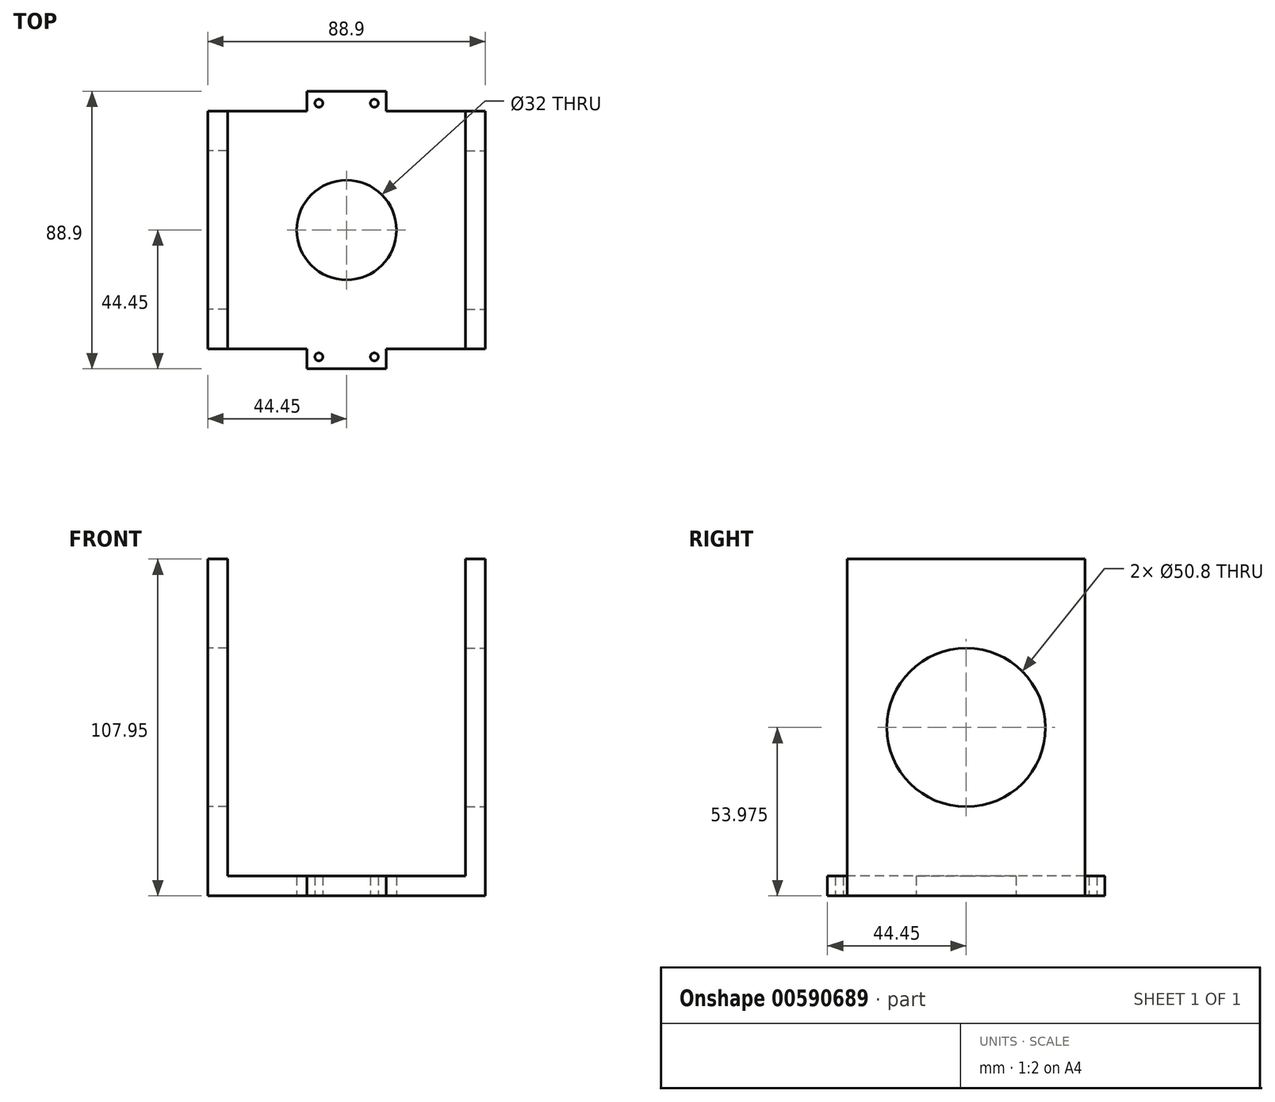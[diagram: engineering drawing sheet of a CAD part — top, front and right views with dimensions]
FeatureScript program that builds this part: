
annotation { "Feature Type Name" : "Feature", "Feature Type Description" : "" }
export const myFeature = defineFeature(function(context is Context, id is Id, definition is map)
    precondition{}
    {
        {
            var Q0;
            Q0=qCreatedBy(makeId("Top.planeOp"),FACE);
            var sketch = newSketch(context, id + "F0", { "sketchPlane" : qUnion([Q0])});
            skLineSegment(sketch, "E0.bottom", {"start": v(0, 0) * mm, "end": v(-88.9, 0) * mm});
            skLineSegment(sketch, "E0.top", {"start": v(0, -76.2) * mm, "end": v(-88.9, -76.2) * mm});
            skLineSegment(sketch, "E0.left", {"start": v(0, 0) * mm, "end": v(0, -76.2) * mm});
            skLineSegment(sketch, "E0.right", {"start": v(-88.9, 0) * mm, "end": v(-88.9, -76.2) * mm});
            skPoint(sketch, "E1.endSnap0", {"position": v(0, -38.1) * mm});
            skCircle(sketch, "E2", {"center": v(-44.45, -38.1) * mm, "radius": 16 * mm});
            skPoint(sketch, "E3.orphan", {"position": v(-44.45, 0) * mm});
            skLineSegment(sketch, "E4", {"start": v(-44.45, -38.1) * mm, "end": v(0, -38.1) * mm});
            skLineSegment(sketch, "E5.bottom", {"start": v(-57.15, 6.35) * mm, "end": v(-31.75, 6.35) * mm});
            skLineSegment(sketch, "E5.left", {"start": v(-57.15, 6.35) * mm, "end": v(-57.15, 0) * mm});
            skLineSegment(sketch, "E5.right", {"start": v(-31.75, 6.35) * mm, "end": v(-31.75, 0) * mm});
            skLineSegment(sketch, "E6.bottom", {"start": v(-57.15, 0) * mm, "end": v(-53.34, 0) * mm});
            skLineSegment(sketch, "E6.top", {"start": v(-54.6, 2.54) * mm, "end": v(-53.34, 2.54) * mm});
            skLineSegment(sketch, "E6.left", {"start": v(-57.15, 0) * mm, "end": v(-57.15, 2.54) * mm});
            skLineSegment(sketch, "E6.right", {"start": v(-53.34, 1.27) * mm, "end": v(-53.34, 2.54) * mm});
            skLineSegment(sketch, "E7.bottom", {"start": v(-31.75, 0) * mm, "end": v(-35.56, 0) * mm});
            skLineSegment(sketch, "E7.top", {"start": v(-34.3, 2.54) * mm, "end": v(-35.56, 2.54) * mm});
            skLineSegment(sketch, "E7.left", {"start": v(-31.75, 0) * mm, "end": v(-31.75, 2.54) * mm});
            skLineSegment(sketch, "E7.right", {"start": v(-35.56, 1.27) * mm, "end": v(-35.56, 2.54) * mm});
            skCircle(sketch, "E8", {"center": v(-53.34, 2.54) * mm, "radius": 1.27 * mm});
            skCircle(sketch, "E9", {"center": v(-35.56, 2.54) * mm, "radius": 1.27 * mm});
            skPoint(sketch, "E10.orphan", {"position": v(-57.15, -6.35) * mm});
            skPoint(sketch, "E11.orphan", {"position": v(-31.75, -6.35) * mm});
            skLineSegment(sketch, "E12.bottom", {"start": v(-31.75, -82.55) * mm, "end": v(-57.15, -82.55) * mm});
            skLineSegment(sketch, "E12.left", {"start": v(-31.75, -82.55) * mm, "end": v(-31.75, -76.2) * mm});
            skLineSegment(sketch, "E12.right", {"start": v(-57.15, -82.55) * mm, "end": v(-57.15, -76.2) * mm});
            skPoint(sketch, "E12.middle", {"position": v(-44.45, -76.2) * mm});
            skLineSegment(sketch, "E13.bottom", {"start": v(-57.15, -76.2) * mm, "end": v(-53.34, -76.2) * mm});
            skLineSegment(sketch, "E13.top", {"start": v(-54.6, -78.74) * mm, "end": v(-53.34, -78.74) * mm});
            skLineSegment(sketch, "E13.left", {"start": v(-57.15, -76.2) * mm, "end": v(-57.15, -78.74) * mm});
            skLineSegment(sketch, "E13.right", {"start": v(-53.34, -77.47) * mm, "end": v(-53.34, -78.74) * mm});
            skLineSegment(sketch, "E14.bottom", {"start": v(-31.75, -76.2) * mm, "end": v(-35.56, -76.2) * mm});
            skLineSegment(sketch, "E14.top", {"start": v(-34.29, -78.74) * mm, "end": v(-35.56, -78.74) * mm});
            skLineSegment(sketch, "E14.left", {"start": v(-31.75, -76.2) * mm, "end": v(-31.75, -78.74) * mm});
            skLineSegment(sketch, "E14.right", {"start": v(-35.56, -77.47) * mm, "end": v(-35.56, -78.74) * mm});
            skCircle(sketch, "E15", {"center": v(-53.34, -78.74) * mm, "radius": 1.27 * mm});
            skCircle(sketch, "E16", {"center": v(-35.56, -78.74) * mm, "radius": 1.27 * mm});
            skPoint(sketch, "E17.orphan", {"position": v(-57.15, -69.85) * mm});
            skPoint(sketch, "E18.orphan", {"position": v(-31.75, -69.85) * mm});
            skSolve(sketch);
        }
        {
            var Q0;
            Q0=makeQuery(id+"F0.imprint","IMPRINT",FACE,{"disambiguationData":[TD([[makeQuery(id+"F0.imprint","IMPRINT",EDGE,{"derivedFrom":sQuery(id+"F0.wireOp",EDGE,"E0.bottom")}),1.0]])]});
            var Q1;
            Q1=makeQuery(id+"F0.imprint","IMPRINT",FACE,{"disambiguationData":[TD([[makeQuery(id+"F0.imprint","IMPRINT",EDGE,{"derivedFrom":sQuery(id+"F0.wireOp",EDGE,"E5.bottom")}),-1.0]])]});
            var Q2;
            Q2=makeQuery(id+"F0.imprint","IMPRINT",FACE,{"disambiguationData":[TD([[makeQuery(id+"F0.imprint","IMPRINT",EDGE,{"derivedFrom":sQuery(id+"F0.wireOp",EDGE,"E12.bottom")}),-1.0]])]});
            extrude(context, id + "F1", {"entities" : qUnion([Q0, Q1, Q2]), "depth" : 6.35 * mm, "offsetDistance" : 25.4 * mm});
        }
        {
            var Q0;
            Q0=makeQuery(id+"F1.opExtrude","CAP_FACE",FACE,{"disambiguationData":[OSD([sQuery(id+"F0.wireOp",EDGE,"E0.bottom"),sQuery(id+"F0.wireOp",EDGE,"E0.top"),sQuery(id+"F0.wireOp",EDGE,"E0.left"),sQuery(id+"F0.wireOp",EDGE,"E0.right"),sQuery(id+"F0.wireOp",EDGE,"E2")])],"isStart":false});
            var sketch = newSketch(context, id + "F2", { "sketchPlane" : qUnion([Q0])});
            skLineSegment(sketch, "E19.bottom", {"start": v(-88.9, 0) * mm, "end": v(-82.55, 0) * mm});
            skLineSegment(sketch, "E19.top", {"start": v(-88.9, -76.2) * mm, "end": v(-82.55, -76.2) * mm});
            skLineSegment(sketch, "E19.left", {"start": v(-88.9, 0) * mm, "end": v(-88.9, -76.2) * mm});
            skLineSegment(sketch, "E19.right", {"start": v(-82.55, 0) * mm, "end": v(-82.55, -76.2) * mm});
            skLineSegment(sketch, "E20.bottom", {"start": v(0, 0) * mm, "end": v(-6.35, 0) * mm});
            skLineSegment(sketch, "E20.top", {"start": v(0, -76.2) * mm, "end": v(-6.35, -76.2) * mm});
            skLineSegment(sketch, "E20.left", {"start": v(0, 0) * mm, "end": v(0, -76.2) * mm});
            skLineSegment(sketch, "E20.right", {"start": v(-6.35, 0) * mm, "end": v(-6.35, -76.2) * mm});
            skSolve(sketch);
        }
        {
            var Q0;
            Q0=makeQuery(id+"F2.imprint","IMPRINT",FACE,{"disambiguationData":[TD([[makeQuery(id+"F2.imprint","IMPRINT",EDGE,{"derivedFrom":sQuery(id+"F2.wireOp",EDGE,"E19.bottom")}),1.0]])]});
            extrude(context, id + "F3", {"entities" : qUnion([Q0]), "operationType" : NewBodyOperationType.ADD, "depth" : 101.6 * mm, "offsetDistance" : 25.4 * mm});
        }
        {
            var Q0;
            Q0=makeQuery(id+"F3.boolean.opBoolean","MERGE",FACE,{"derivedFrom":[makeQuery(id+"F1.opExtrude","SWEPT_FACE",FACE,{"disambiguationData":[OSD([sQuery(id+"F0.wireOp",EDGE,"E0.right")])]}),makeQuery(id+"F3.opExtrude","SWEPT_FACE",FACE,{"disambiguationData":[OSD([sQuery(id+"F2.wireOp",EDGE,"E19.left")])]})]});
            var sketch = newSketch(context, id + "F4", { "sketchPlane" : qUnion([Q0])});
            skPoint(sketch, "E21.endSnap0", {"position": v(0, 53.97) * mm});
            skCircle(sketch, "E22", {"center": v(38.1, 53.97) * mm, "radius": 25.4 * mm});
            skPoint(sketch, "E21.start.orphan", {"position": v(38.1, 107.95) * mm});
            skLineSegment(sketch, "E23", {"start": v(0, 53.97) * mm, "end": v(38.1, 53.97) * mm});
            skSolve(sketch);
        }
        {
            var Q0;
            Q0=makeQuery(id+"F4.imprint","IMPRINT",FACE,{"disambiguationData":[TD([[makeQuery(id+"F4.imprint","IMPRINT",EDGE,{"derivedFrom":sQuery(id+"F4.wireOp",EDGE,"E22")}),1.0]])]});
            extrude(context, id + "F5", {"entities" : qUnion([Q0]), "operationType" : NewBodyOperationType.REMOVE, "oppositeDirection" : true, "depth" : 101.6 * mm, "offsetDistance" : 25.4 * mm});
        }
        {
            var Q0;
            Q0=makeQuery(id+"F1.opExtrude","CAP_FACE",FACE,{"disambiguationData":[OSD([sQuery(id+"F0.wireOp",EDGE,"E0.bottom"),sQuery(id+"F0.wireOp",EDGE,"E0.top"),sQuery(id+"F0.wireOp",EDGE,"E0.left"),sQuery(id+"F0.wireOp",EDGE,"E0.right"),sQuery(id+"F0.wireOp",EDGE,"E2")])],"isStart":false});
            var sketch = newSketch(context, id + "F6", { "sketchPlane" : qUnion([Q0])});
            skLineSegment(sketch, "E24.bottom", {"start": v(0, 0) * mm, "end": v(-6.35, 0) * mm});
            skLineSegment(sketch, "E24.top", {"start": v(0, -76.2) * mm, "end": v(-6.35, -76.2) * mm});
            skLineSegment(sketch, "E24.left", {"start": v(0, 0) * mm, "end": v(0, -76.2) * mm});
            skLineSegment(sketch, "E24.right", {"start": v(-6.35, 0) * mm, "end": v(-6.35, -76.2) * mm});
            skSolve(sketch);
        }
        {
            var Q0;
            Q0=makeQuery(id+"F6.imprint","IMPRINT",FACE,{"disambiguationData":[TD([[makeQuery(id+"F6.imprint","IMPRINT",EDGE,{"derivedFrom":sQuery(id+"F6.wireOp",EDGE,"E24.bottom")}),1.0]])]});
            extrude(context, id + "F7", {"entities" : qUnion([Q0]), "operationType" : NewBodyOperationType.ADD, "depth" : 101.6 * mm, "offsetDistance" : 25.4 * mm});
        }
        {
            var Q0;
            Q0=makeQuery(id+"F7.boolean.opBoolean","MERGE",FACE,{"derivedFrom":[makeQuery(id+"F1.opExtrude","SWEPT_FACE",FACE,{"disambiguationData":[OSD([sQuery(id+"F0.wireOp",EDGE,"E0.left")])]}),makeQuery(id+"F7.opExtrude","SWEPT_FACE",FACE,{"disambiguationData":[OSD([sQuery(id+"F6.wireOp",EDGE,"E24.left")])]})]});
            var sketch = newSketch(context, id + "F8", { "sketchPlane" : qUnion([Q0])});
            skLineSegment(sketch, "E25", {"start": v(-38.1, 107.95) * mm, "end": v(-38.1, 53.97) * mm});
            skPoint(sketch, "E25.endSnap0", {"position": v(-76.2, 53.97) * mm});
            skCircle(sketch, "E26", {"center": v(-38.1, 53.97) * mm, "radius": 25.4 * mm});
            skSolve(sketch);
        }
        {
            var Q0;
            Q0=makeQuery(id+"F8.imprint","IMPRINT",FACE,{"disambiguationData":[TD([[makeQuery(id+"F8.imprint","IMPRINT",EDGE,{"derivedFrom":sQuery(id+"F8.wireOp",EDGE,"E26")}),1.0]])]});
            extrude(context, id + "F9", {"entities" : qUnion([Q0]), "operationType" : NewBodyOperationType.REMOVE, "oppositeDirection" : true, "depth" : 25.4 * mm, "offsetDistance" : 25.4 * mm});
        }
    });
